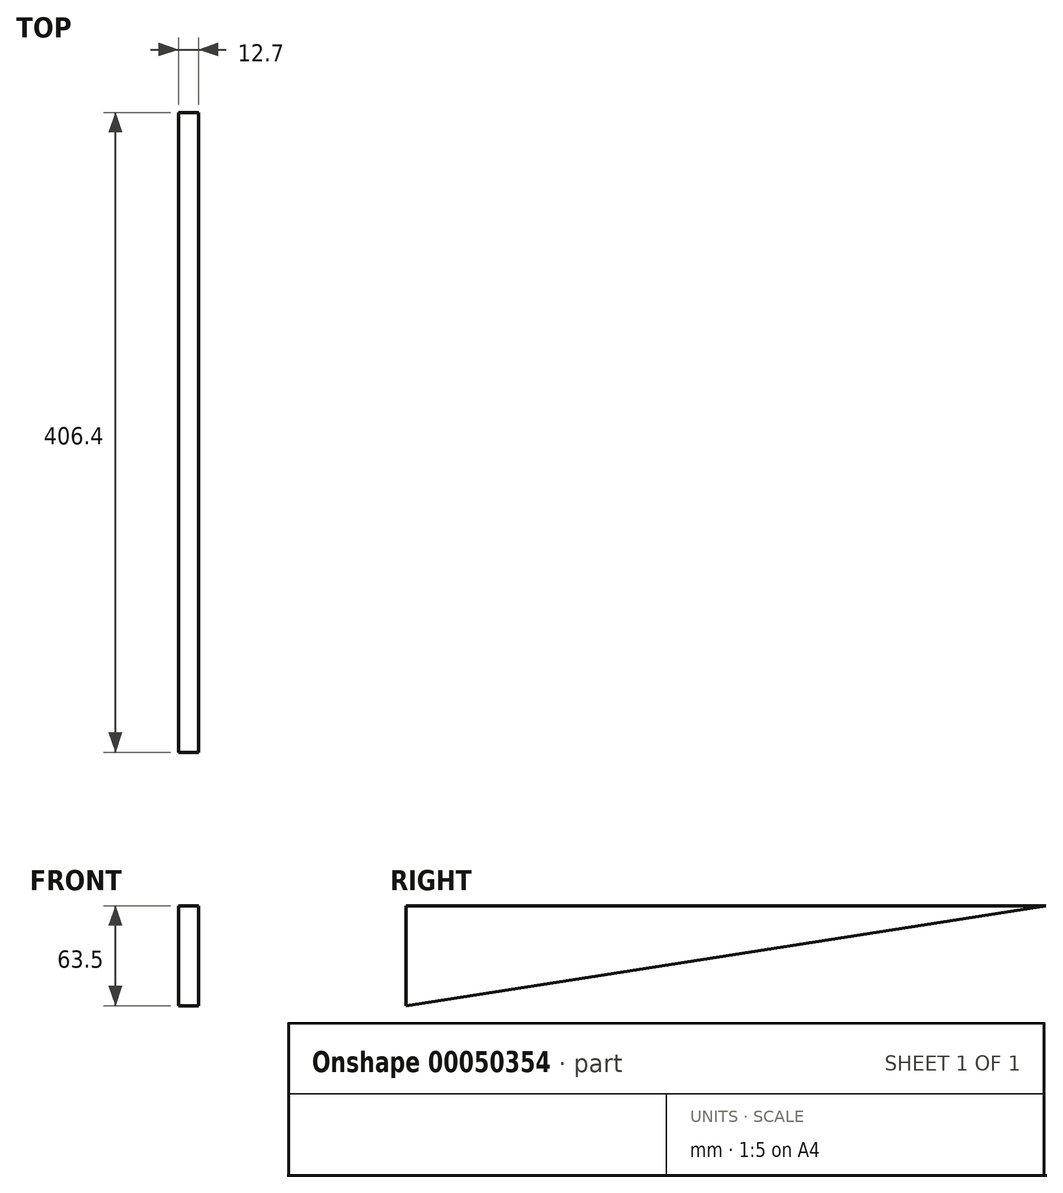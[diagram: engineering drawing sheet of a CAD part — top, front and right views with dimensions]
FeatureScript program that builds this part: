
annotation { "Feature Type Name" : "Feature", "Feature Type Description" : "" }
export const myFeature = defineFeature(function(context is Context, id is Id, definition is map)
    precondition{}
    {
        {
            var Q0;
            Q0=qCreatedBy(makeId("Right.planeOp"),FACE);
            var sketch = newSketch(context, id + "F0", { "sketchPlane" : qUnion([Q0])});
            skLineSegment(sketch, "E0", {"start": v(-226.31, -41.79) * mm, "end": v(180.09, -41.79) * mm});
            skLineSegment(sketch, "E1", {"start": v(-226.31, -41.79) * mm, "end": v(-226.31, -105.29) * mm});
            skLineSegment(sketch, "E2", {"start": v(-226.31, -105.29) * mm, "end": v(180.09, -41.79) * mm});
            skSolve(sketch);
        }
        {
            var Q0;
            Q0 = qSketchRegion(id + "F0", true);
            extrude(context, id + "F1", {"entities" : qUnion([Q0]), "depth" : 12.7 * mm});
        }
    });
